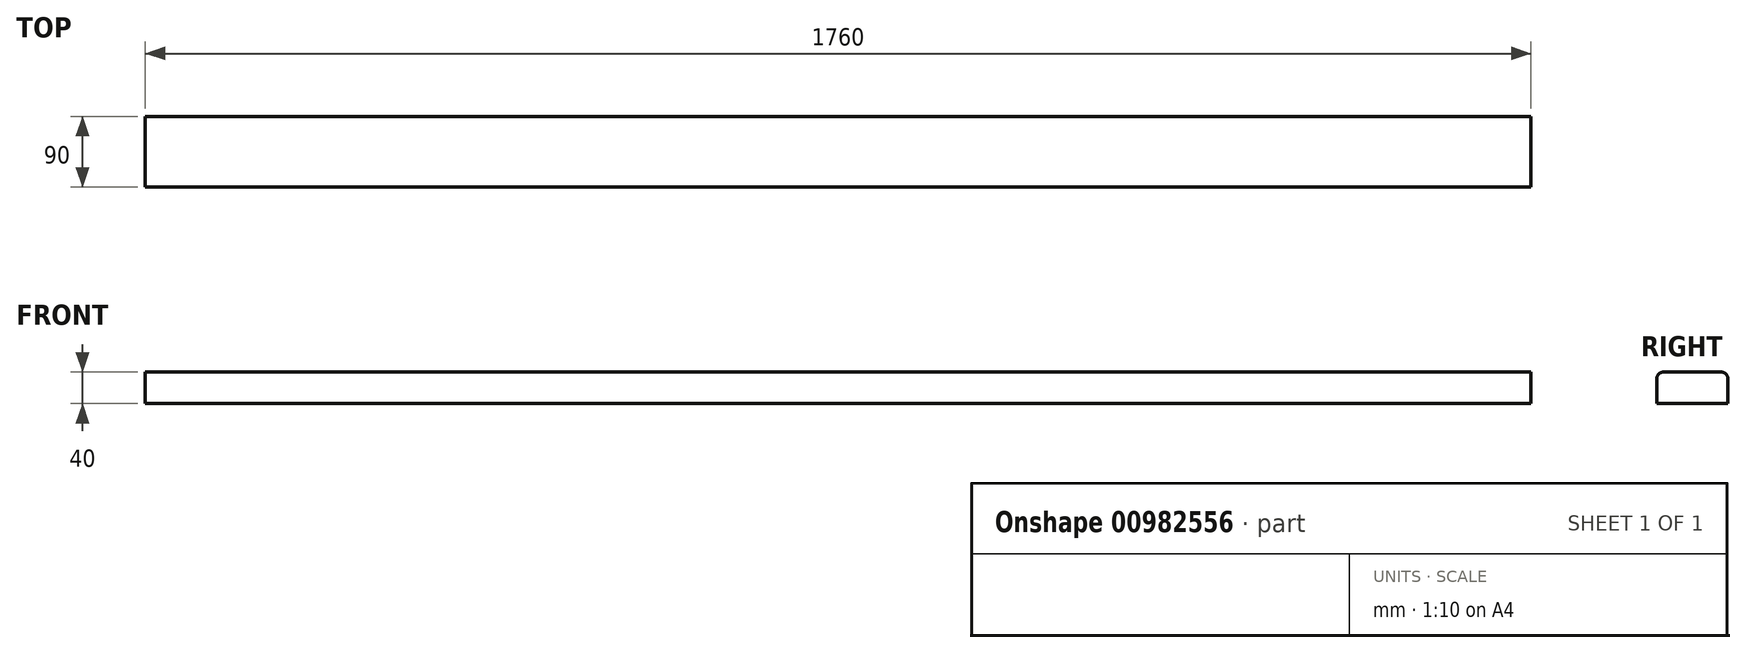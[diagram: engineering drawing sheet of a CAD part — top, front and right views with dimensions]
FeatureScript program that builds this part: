
annotation { "Feature Type Name" : "Feature", "Feature Type Description" : "" }
export const myFeature = defineFeature(function(context is Context, id is Id, definition is map)
    precondition{}
    {
        {
            var Q0;
            Q0=qCreatedBy(makeId("Right.planeOp"),FACE);
            var sketch = newSketch(context, id + "F0", { "sketchPlane" : qUnion([Q0])});
            skLineSegment(sketch, "E0", {"start": v(0, 0) * mm, "end": v(-90, 0) * mm});
            skLineSegment(sketch, "E1", {"start": v(-90, 0) * mm, "end": v(-90, 32) * mm});
            skLineSegment(sketch, "E2", {"start": v(-82, 40) * mm, "end": v(-8, 40) * mm});
            skLineSegment(sketch, "E3", {"start": v(0, 32) * mm, "end": v(0, 0) * mm});
            skPoint(sketch, "E4.visualSharp", {"position": v(-90, 40) * mm});
            skArc(sketch, "E4.filletArc", {"start": v(-82, 40) * mm, "mid": v(-87.66, 37.66) * mm, "end": v(-90, 32) * mm});
            skPoint(sketch, "E5.visualSharp", {"position": v(0, 40) * mm});
            skArc(sketch, "E5.filletArc", {"start": v(0, 32) * mm, "mid": v(-2.34, 37.66) * mm, "end": v(-8, 40) * mm});
            skSolve(sketch);
        }
        {
            var Q0;
            Q0=makeQuery(id+"F0.imprint","IMPRINT",FACE,{"disambiguationData":[TD([[makeQuery(id+"F0.imprint","IMPRINT",EDGE,{"derivedFrom":sQuery(id+"F0.wireOp",EDGE,"E0")}),-1.0]])]});
            extrude(context, id + "F1", {"entities" : qUnion([Q0]), "endBound" : BoundingType.SYMMETRIC, "depth" : 1760 * mm, "offsetDistance" : 25 * mm});
        }
    });
